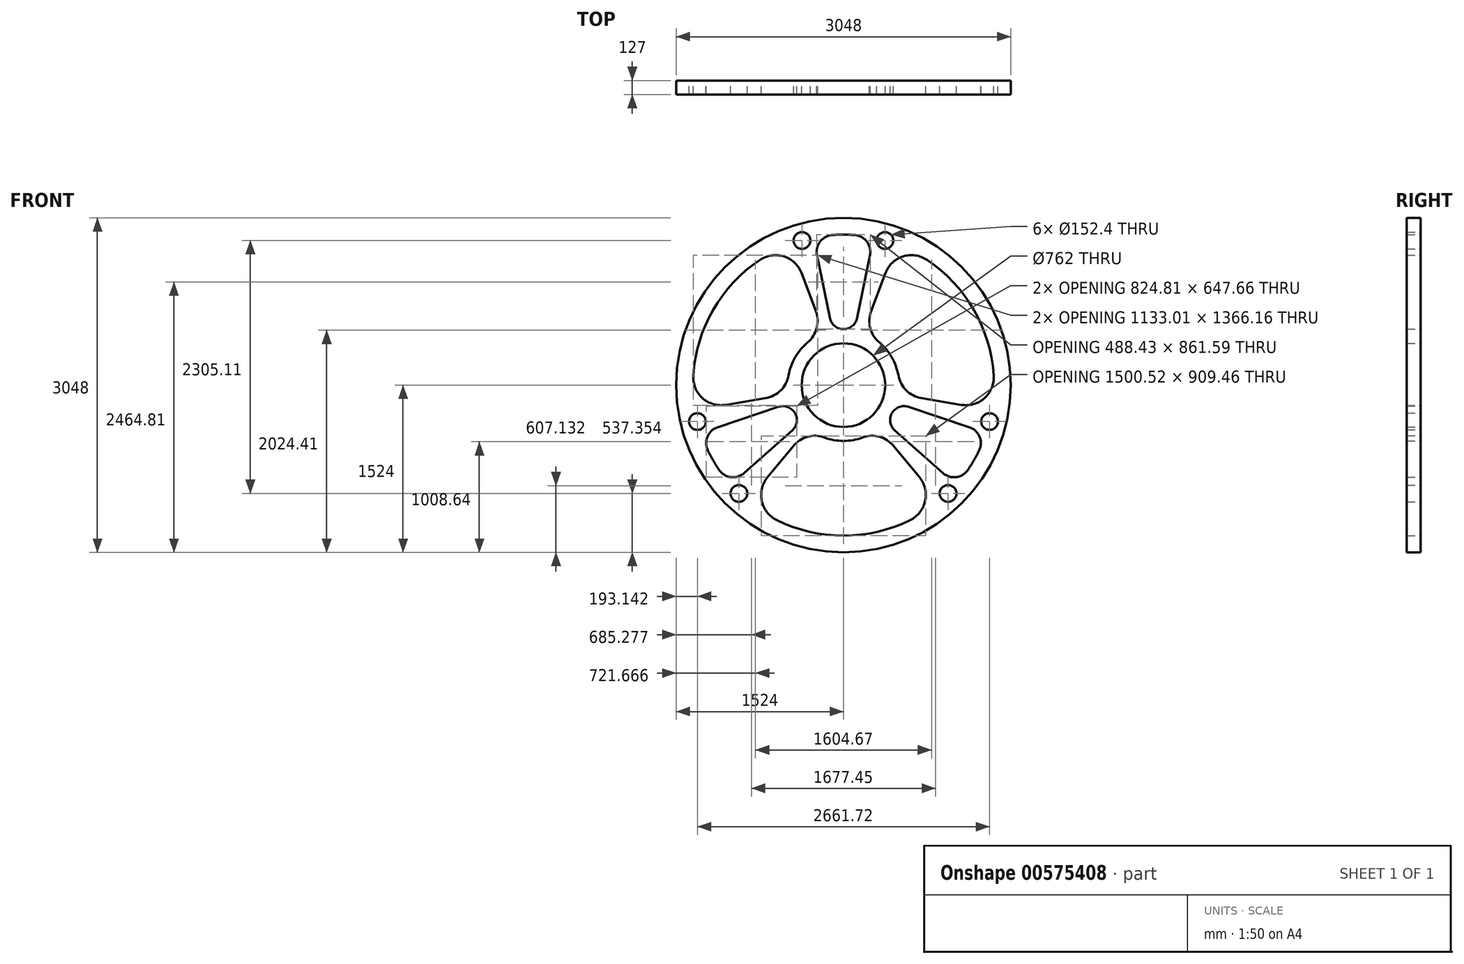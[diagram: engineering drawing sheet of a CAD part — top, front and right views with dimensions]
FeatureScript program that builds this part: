
annotation { "Feature Type Name" : "Feature", "Feature Type Description" : "" }
export const myFeature = defineFeature(function(context is Context, id is Id, definition is map)
    precondition{}
    {
        {
            var Q0;
            Q0=qCreatedBy(makeId("Front.planeOp"),FACE);
            var sketch = newSketch(context, id + "F0", { "sketchPlane" : qUnion([Q0])});
            skCircle(sketch, "E0", {"center": v(0, 0) * mm, "radius": 1524 * mm});
            skArc(sketch, "E1", {"start": v(103.3, 1367.7) * mm, "mid": v(0, 1371.6) * mm, "end": v(-103.3, 1367.7) * mm});
            skCircle(sketch, "E2", {"center": v(-378.06, 1318.47) * mm, "radius": 76.2 * mm});
            skCircle(sketch, "E3", {"center": v(378.06, 1318.47) * mm, "radius": 76.2 * mm});
            skCircle(sketch, "E4", {"center": v(0, 0) * mm, "radius": 381 * mm});
            skArc(sketch, "E5.trimOffspring", {"start": v(-103.3, 1367.7) * mm, "mid": v(-213.39, 1307.65) * mm, "end": v(-241.16, 1185.35) * mm});
            skArc(sketch, "E6.trimOffspring", {"start": v(241.16, 1185.35) * mm, "mid": v(213.39, 1307.65) * mm, "end": v(103.3, 1367.7) * mm});
            skLineSegment(sketch, "E7.trimOffspring", {"start": v(-124.45, 611.7) * mm, "end": v(-241.16, 1185.35) * mm});
            skLineSegment(sketch, "E8.trimOffspring", {"start": v(124.45, 611.7) * mm, "end": v(241.16, 1185.35) * mm});
            skArc(sketch, "E9", {"start": v(-173.99, -477.28) * mm, "mid": v(0, -508) * mm, "end": v(173.99, -477.28) * mm});
            skArc(sketch, "E10", {"start": v(-124.45, 611.7) * mm, "mid": v(0, 510.01) * mm, "end": v(124.45, 611.7) * mm});
            skPoint(sketch, "E11.endSnap0", {"position": v(0, -1371.6) * mm});
            skArc(sketch, "E12", {"start": v(609.08, -1228.95) * mm, "mid": v(744.67, -1054.47) * mm, "end": v(692.28, -839.8) * mm});
            skArc(sketch, "E13.trimOffspring", {"start": v(-173.99, -477.28) * mm, "mid": v(-327.73, -470.84) * mm, "end": v(-456.97, -554.35) * mm});
            skLineSegment(sketch, "E14.trimOffspring", {"start": v(-456.97, -554.35) * mm, "end": v(-692.28, -839.8) * mm});
            skArc(sketch, "E15.trimOffspring", {"start": v(-609.08, -1228.95) * mm, "mid": v(0, -1371.6) * mm, "end": v(609.08, -1228.95) * mm});
            skArc(sketch, "E16.trimOffspring", {"start": v(-692.28, -839.8) * mm, "mid": v(-744.67, -1054.47) * mm, "end": v(-609.08, -1228.95) * mm});
            skLineSegment(sketch, "E17.trimOffspring", {"start": v(456.97, -554.35) * mm, "end": v(692.28, -839.8) * mm});
            skArc(sketch, "E18.trimOffspring", {"start": v(456.97, -554.35) * mm, "mid": v(327.73, -470.84) * mm, "end": v(173.99, -477.28) * mm});
            skArc(sketch, "E19.1.0", {"start": v(500.33, 87.96) * mm, "mid": v(439.94, 254) * mm, "end": v(326.34, 389.31) * mm});
            skArc(sketch, "E19.1.1", {"start": v(500.33, 87.96) * mm, "mid": v(571.62, -48.4) * mm, "end": v(708.57, -118.57) * mm});
            skLineSegment(sketch, "E19.1.2", {"start": v(708.57, -118.57) * mm, "end": v(1073.43, -179.63) * mm});
            skArc(sketch, "E19.1.3", {"start": v(1073.43, -179.63) * mm, "mid": v(1285.53, -117.67) * mm, "end": v(1368.84, 87) * mm});
            skArc(sketch, "E19.1.4", {"start": v(1368.84, 87) * mm, "mid": v(1187.84, 685.8) * mm, "end": v(759.76, 1141.95) * mm});
            skArc(sketch, "E19.1.5", {"start": v(759.76, 1141.95) * mm, "mid": v(540.86, 1172.14) * mm, "end": v(381.15, 1019.43) * mm});
            skLineSegment(sketch, "E19.1.6", {"start": v(251.6, 672.92) * mm, "end": v(381.15, 1019.43) * mm});
            skArc(sketch, "E19.1.7", {"start": v(251.6, 672.92) * mm, "mid": v(243.9, 519.24) * mm, "end": v(326.34, 389.31) * mm});
            skArc(sketch, "E19.2.0", {"start": v(-326.34, 389.31) * mm, "mid": v(-439.94, 254) * mm, "end": v(-500.33, 87.96) * mm});
            skArc(sketch, "E19.2.1", {"start": v(-326.34, 389.31) * mm, "mid": v(-243.9, 519.24) * mm, "end": v(-251.6, 672.92) * mm});
            skLineSegment(sketch, "E19.2.2", {"start": v(-251.6, 672.92) * mm, "end": v(-381.15, 1019.43) * mm});
            skArc(sketch, "E19.2.3", {"start": v(-381.15, 1019.43) * mm, "mid": v(-540.86, 1172.14) * mm, "end": v(-759.76, 1141.95) * mm});
            skArc(sketch, "E19.2.4", {"start": v(-759.76, 1141.95) * mm, "mid": v(-1187.84, 685.8) * mm, "end": v(-1368.84, 87) * mm});
            skArc(sketch, "E19.2.5", {"start": v(-1368.84, 87) * mm, "mid": v(-1285.53, -117.67) * mm, "end": v(-1073.43, -179.63) * mm});
            skLineSegment(sketch, "E19.2.6", {"start": v(-708.57, -118.57) * mm, "end": v(-1073.43, -179.63) * mm});
            skArc(sketch, "E19.2.7", {"start": v(-708.57, -118.57) * mm, "mid": v(-571.62, -48.4) * mm, "end": v(-500.33, 87.96) * mm});
            skCircle(sketch, "E20.1.0", {"center": v(-1330.86, -331.82) * mm, "radius": 76.2 * mm});
            skArc(sketch, "E20.1.1", {"start": v(-1147.13, -383.82) * mm, "mid": v(-1239.15, -469.02) * mm, "end": v(-1236.12, -594.4) * mm});
            skArc(sketch, "E20.1.2", {"start": v(-1236.12, -594.4) * mm, "mid": v(-1187.84, -685.8) * mm, "end": v(-1132.82, -773.31) * mm});
            skArc(sketch, "E20.1.3", {"start": v(-1132.82, -773.31) * mm, "mid": v(-1025.76, -838.62) * mm, "end": v(-905.96, -801.53) * mm});
            skLineSegment(sketch, "E20.1.4", {"start": v(-467.52, -413.62) * mm, "end": v(-905.96, -801.53) * mm});
            skArc(sketch, "E20.1.5", {"start": v(-467.52, -413.62) * mm, "mid": v(-441.68, -255) * mm, "end": v(-591.97, -198.07) * mm});
            skLineSegment(sketch, "E20.1.6", {"start": v(-591.97, -198.07) * mm, "end": v(-1147.13, -383.82) * mm});
            skCircle(sketch, "E20.1.7", {"center": v(-952.8, -986.65) * mm, "radius": 76.2 * mm});
            skCircle(sketch, "E20.2.0", {"center": v(952.8, -986.65) * mm, "radius": 76.2 * mm});
            skArc(sketch, "E20.2.1", {"start": v(905.96, -801.53) * mm, "mid": v(1025.76, -838.62) * mm, "end": v(1132.82, -773.31) * mm});
            skArc(sketch, "E20.2.2", {"start": v(1132.82, -773.31) * mm, "mid": v(1187.84, -685.8) * mm, "end": v(1236.12, -594.4) * mm});
            skArc(sketch, "E20.2.3", {"start": v(1236.12, -594.4) * mm, "mid": v(1239.15, -469.02) * mm, "end": v(1147.13, -383.82) * mm});
            skLineSegment(sketch, "E20.2.4", {"start": v(591.97, -198.07) * mm, "end": v(1147.13, -383.82) * mm});
            skArc(sketch, "E20.2.5", {"start": v(591.97, -198.07) * mm, "mid": v(441.68, -255) * mm, "end": v(467.52, -413.62) * mm});
            skLineSegment(sketch, "E20.2.6", {"start": v(467.52, -413.62) * mm, "end": v(905.96, -801.53) * mm});
            skCircle(sketch, "E20.2.7", {"center": v(1330.86, -331.82) * mm, "radius": 76.2 * mm});
            skSolve(sketch);
        }
        {
            var Q0;
            Q0=makeQuery(id+"F0.imprint","IMPRINT",FACE,{"disambiguationData":[TD([[makeQuery(id+"F0.imprint","IMPRINT",EDGE,{"derivedFrom":sQuery(id+"F0.wireOp",EDGE,"E0")}),1.0]])]});
            extrude(context, id + "F1", {"entities" : qUnion([Q0]), "depth" : 127 * mm, "offsetDistance" : 25.4 * mm});
        }
    });
